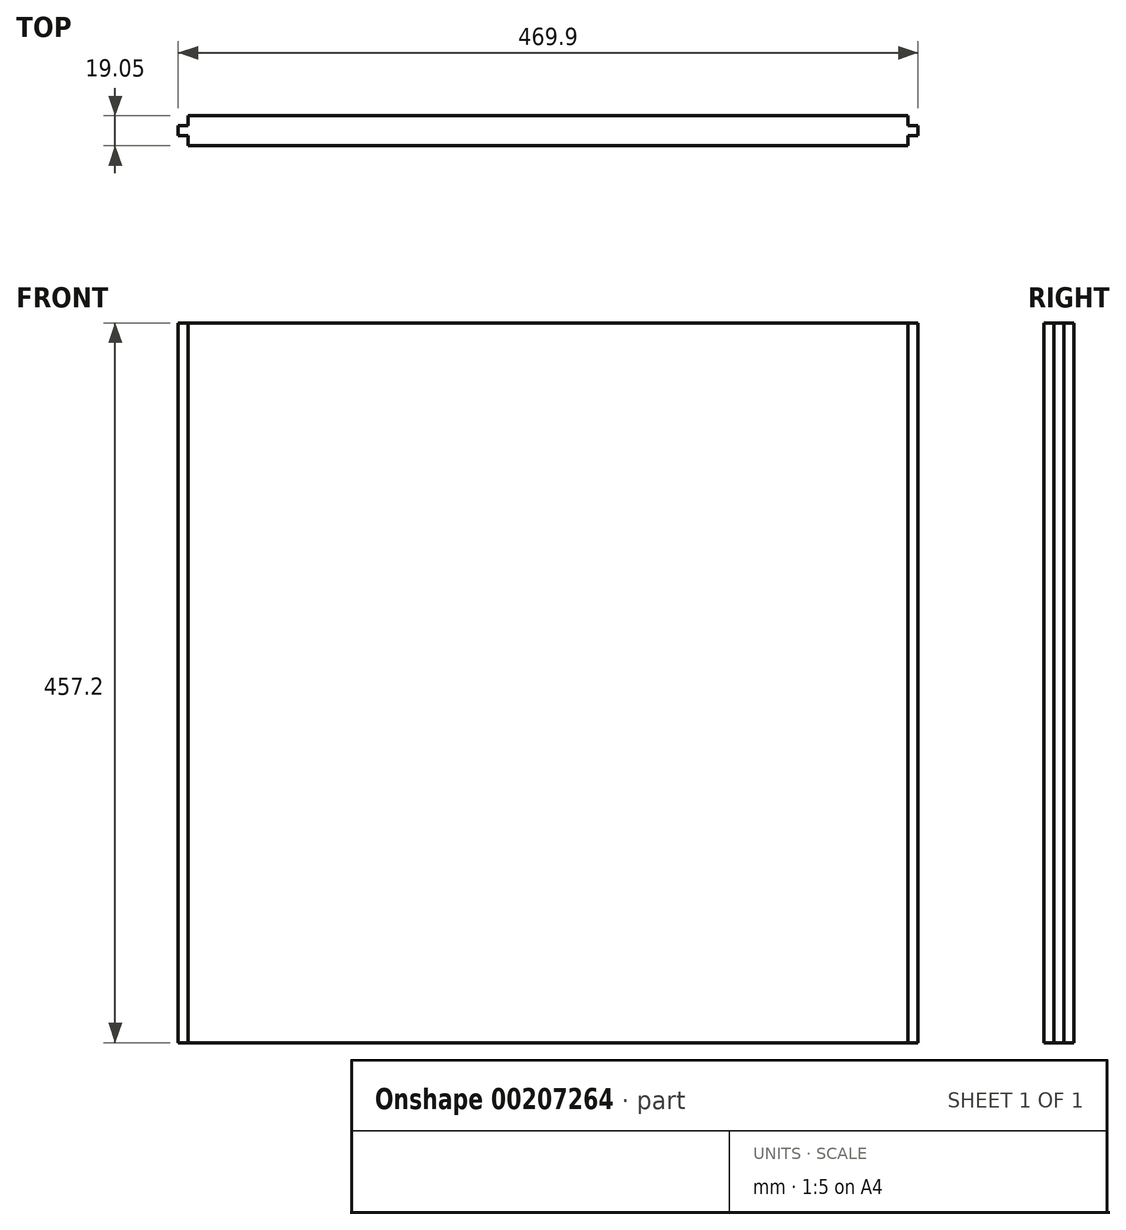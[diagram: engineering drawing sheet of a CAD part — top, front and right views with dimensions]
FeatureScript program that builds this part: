
annotation { "Feature Type Name" : "Feature", "Feature Type Description" : "" }
export const myFeature = defineFeature(function(context is Context, id is Id, definition is map)
    precondition{}
    {
        {
            var Q0;
            Q0=qCreatedBy(makeId("Top.planeOp"),FACE);
            var sketch = newSketch(context, id + "F0", { "sketchPlane" : qUnion([Q0])});
            skLineSegment(sketch, "E0", {"start": v(0, 0) * mm, "end": v(-6.35, 0) * mm});
            skLineSegment(sketch, "E1", {"start": v(-6.35, 0) * mm, "end": v(-6.35, -6.35) * mm});
            skLineSegment(sketch, "E2", {"start": v(-6.35, -6.35) * mm, "end": v(0, -6.35) * mm});
            skLineSegment(sketch, "E3", {"start": v(0, -6.35) * mm, "end": v(0, -12.7) * mm});
            skLineSegment(sketch, "E4", {"start": v(0, -12.7) * mm, "end": v(457.2, -12.7) * mm});
            skLineSegment(sketch, "E5", {"start": v(457.2, -12.7) * mm, "end": v(457.2, -6.35) * mm});
            skLineSegment(sketch, "E6", {"start": v(457.2, -6.35) * mm, "end": v(463.55, -6.35) * mm});
            skLineSegment(sketch, "E7", {"start": v(463.55, -6.35) * mm, "end": v(463.55, 0) * mm});
            skLineSegment(sketch, "E8", {"start": v(463.55, 0) * mm, "end": v(457.2, 0) * mm});
            skLineSegment(sketch, "E9", {"start": v(457.2, 0) * mm, "end": v(457.2, 6.35) * mm});
            skLineSegment(sketch, "E10", {"start": v(457.2, 6.35) * mm, "end": v(0, 6.35) * mm});
            skLineSegment(sketch, "E11", {"start": v(0, 6.35) * mm, "end": v(0, 0) * mm});
            skSolve(sketch);
        }
        {
            var Q0;
            Q0=makeQuery(id+"F0.imprint","IMPRINT",FACE,{"disambiguationData":[TD([[makeQuery(id+"F0.imprint","IMPRINT",EDGE,{"derivedFrom":sQuery(id+"F0.wireOp",EDGE,"E0")}),1.0]])]});
            extrude(context, id + "F1", {"entities" : qUnion([Q0]), "depth" : 457.2 * mm});
        }
    });
